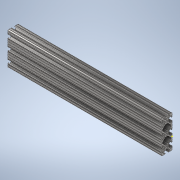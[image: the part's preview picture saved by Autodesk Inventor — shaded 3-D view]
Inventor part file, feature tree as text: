
AUTODESK INVENTOR PART (.ipt)
format: ipt  version: 2020 (Build 240168000, 168)  size: 378,880 bytes
history: native  units: in
note: dims shown in document units (in); Inventor stores cm internally (conversion verified against a paired STEP export)
features: sketch x2, extrude x1
ambient origin geometry x8: Origin, YZ Plane, XZ Plane, XY Plane, X Axis, Y Axis, Z Axis, Center Point
bodies: Solid1 (feature_tree)
feature tree (3):
  extrude  "Extrusion1"  [1 undecoded]
  sketch  "Sketch2"
  sketch  "Sketch1"  dims[d0=14.0in d1=0.0in]
note: 1 required parameter value undecoded (feature->parameter linkage not recoverable at this tier; creation-order binding heuristic only, values carry confidence <= 0.55)
